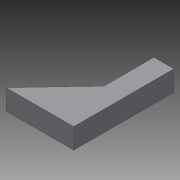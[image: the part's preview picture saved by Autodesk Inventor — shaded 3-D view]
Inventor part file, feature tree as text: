
AUTODESK INVENTOR PART (.ipt)
format: ipt  version: 2015 SP1 (Build 190203100, 203)  size: 67,072 bytes
history: native  units: in
note: dims shown in document units (in); Inventor stores cm internally (conversion verified against a paired STEP export)
features: extrude x1, sketch x1
ambient origin geometry x8: Origin, YZ Plane, XZ Plane, XY Plane, X Axis, Y Axis, Z Axis, Center Point
bodies: Solid1 (feature_tree)
feature tree (2):
  extrude  "Extrusion1"  [1 undecoded]
  sketch  "Sketch1"  dims[d0=0.1in d1=0.0in]
note: 1 required parameter value undecoded (feature->parameter linkage not recoverable at this tier; creation-order binding heuristic only, values carry confidence <= 0.55)
